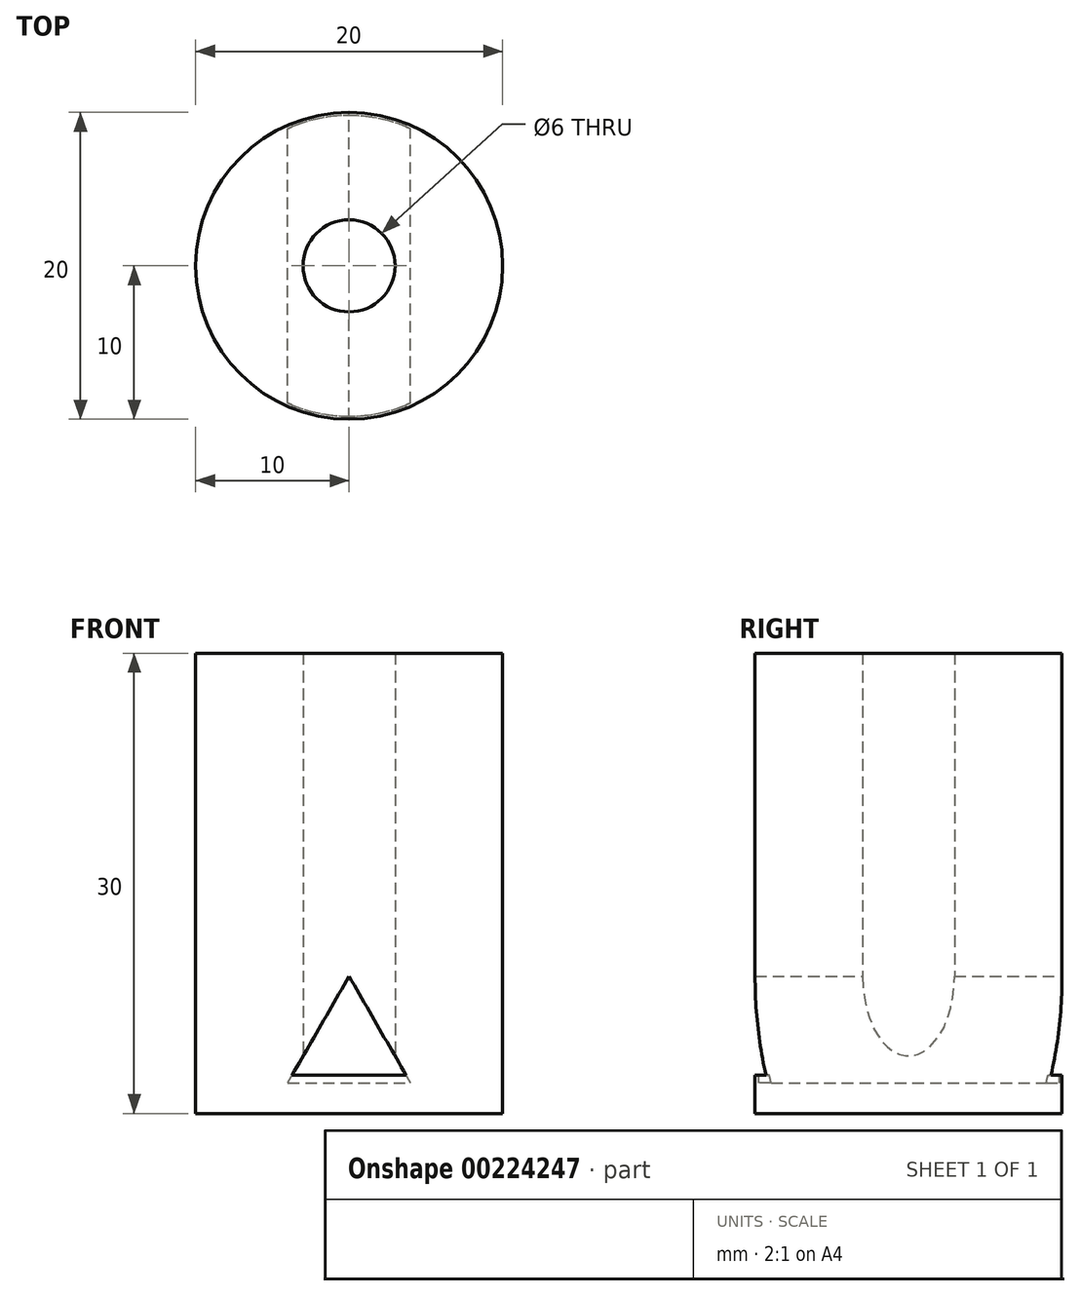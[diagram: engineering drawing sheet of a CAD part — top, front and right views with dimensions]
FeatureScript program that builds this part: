
annotation { "Feature Type Name" : "Feature", "Feature Type Description" : "" }
export const myFeature = defineFeature(function(context is Context, id is Id, definition is map)
    precondition{}
    {
        {
            var Q0;
            Q0=qCreatedBy(makeId("Top.planeOp"),FACE);
            var sketch = newSketch(context, id + "F0", { "sketchPlane" : qUnion([Q0])});
            skCircle(sketch, "E0", {"center": v(0, 0) * mm, "radius": 10 * mm});
            skCircle(sketch, "E1", {"center": v(0, 0) * mm, "radius": 3 * mm});
            skCircle(sketch, "E2", {"center": v(0, 0) * mm, "radius": 9.8 * mm});
            skSolve(sketch);
        }
        {
            var Q0;
            Q0=qCreatedBy(makeId("Front.planeOp"),FACE);
            var sketch = newSketch(context, id + "F1", { "sketchPlane" : qUnion([Q0])});
            skLineSegment(sketch, "E3", {"start": v(0, 2) * mm, "end": v(4, 2) * mm});
            skLineSegment(sketch, "E4", {"start": v(4, 2) * mm, "end": v(0, 8.93) * mm});
            skLineSegment(sketch, "E5", {"start": v(0, 8.93) * mm, "end": v(-4, 2) * mm});
            skLineSegment(sketch, "E6", {"start": v(-4, 2) * mm, "end": v(0, 2) * mm});
            skSolve(sketch);
        }
        {
            var Q0;
            Q0 = qSketchRegion(id + "F0", true);
            var Q1;
            Q1=makeQuery(id+"F0.imprint","IMPRINT",FACE,{"disambiguationData":[TD([[makeQuery(id+"F0.imprint","IMPRINT",EDGE,{"derivedFrom":sQuery(id+"F0.wireOp",EDGE,"E1")}),1.0]])]});
            var Q2;
            Q2=makeQuery(id+"F0.imprint","IMPRINT",FACE,{"disambiguationData":[TD([[makeQuery(id+"F0.imprint","IMPRINT",EDGE,{"derivedFrom":sQuery(id+"F0.wireOp",EDGE,"E1")}),-1.0]])]});
            extrude(context, id + "F2", {"entities" : qUnion([Q0, Q1, Q2]), "depth" : 2 * mm});
        }
        {
            var Q0;
            Q0=makeQuery(id+"F0.imprint","IMPRINT",FACE,{"disambiguationData":[TD([[makeQuery(id+"F0.imprint","IMPRINT",EDGE,{"derivedFrom":sQuery(id+"F0.wireOp",EDGE,"E0")}),1.0]])]});
            var Q1;
            Q1=makeQuery(id+"F0.imprint","IMPRINT",FACE,{"disambiguationData":[TD([[makeQuery(id+"F0.imprint","IMPRINT",EDGE,{"derivedFrom":sQuery(id+"F0.wireOp",EDGE,"E1")}),-1.0]])]});
            extrude(context, id + "F3", {"entities" : qUnion([Q0, Q1]), "operationType" : NewBodyOperationType.ADD, "depth" : 30 * mm});
        }
        {
            var Q0;
            Q0=makeQuery(id+"F1.imprint","IMPRINT",FACE,{"disambiguationData":[TD([[makeQuery(id+"F1.imprint","IMPRINT",EDGE,{"derivedFrom":sQuery(id+"F1.wireOp",EDGE,"E3")}),1.0]])]});
            extrude(context, id + "F4", {"entities" : qUnion([Q0]), "operationType" : NewBodyOperationType.REMOVE, "depth" : 25 * mm, "hasSecondDirection" : true, "secondDirectionOppositeDirection" : true, "secondDirectionDepth" : 25 * mm});
        }
        {
            var Q0;
            Q0=makeQuery(id+"F0.imprint","IMPRINT",FACE,{"disambiguationData":[TD([[makeQuery(id+"F0.imprint","IMPRINT",EDGE,{"derivedFrom":sQuery(id+"F0.wireOp",EDGE,"E0")}),1.0]])]});
            extrude(context, id + "F5", {"entities" : qUnion([Q0]), "operationType" : NewBodyOperationType.ADD, "depth" : 2.5 * mm});
        }
    });
